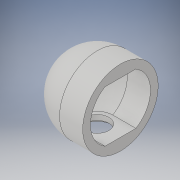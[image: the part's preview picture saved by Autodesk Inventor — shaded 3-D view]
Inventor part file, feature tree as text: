
AUTODESK INVENTOR PART (.ipt)
format: ipt  version: 2017 (Build 210142000, 142)  size: 185,856 bytes
history: native  units: in
note: dims shown in document units (in); Inventor stores cm internally (conversion verified against a paired STEP export)
features: sketch x5, extrude x2, other x1, sweep x1, plane x1
ambient origin geometry x8: Origin, YZ Plane, XZ Plane, XY Plane, X Axis, Y Axis, Z Axis, Center Point
bodies: Solid1 (feature_tree)
feature tree (10):
  other  "way down"
  extrude  "corridor"  Depth=1.0in
  sweep  "end dome"
  plane  "Work Plane1"
  extrude  "connection for pipe"  Depth=2.0in TaperAngle=0.0deg
  sketch  "Sketch1"  dims[d0=6.6667in d1=4.0in d2=2.0in d3=0.0in d6=1.0in]
  sketch  "Sketch2"  dims[d7=1.0in d8=0.0in d9=0.0in]
  sketch  "Sketch3"  dims[d10=3.0in d11=2.0in d12=0.0in]
  sketch  "Sketch4"  dims[d13=-5.0in]
  sketch  "Sketch5"  dims[d14=4.0in d15=1.0in d16=0.0in]
